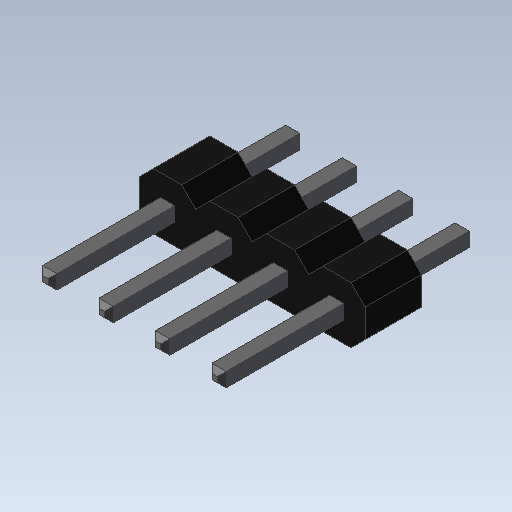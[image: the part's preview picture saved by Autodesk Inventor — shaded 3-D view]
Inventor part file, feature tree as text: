
AUTODESK INVENTOR PART (.ipt)
format: ipt  version: 2020 (Build 240168000, 168)  size: 143,360 bytes
history: imported  units: in
note: dims shown in document units (in); Inventor stores cm internally (conversion verified against a paired STEP export)
features: imported_body x1
ambient origin geometry x8: Origin, YZ Plane, XZ Plane, XY Plane, X Axis, Y Axis, Z Axis, Center Point
bodies: Solid1 (imported_parasolid), Body2 (imported_parasolid)
feature tree (1):
  imported_body  NMx_Import_Brep_tag  [imported B-rep: ~100 faces, bbox_mm=[10.16, 2.54, 11.34]]
